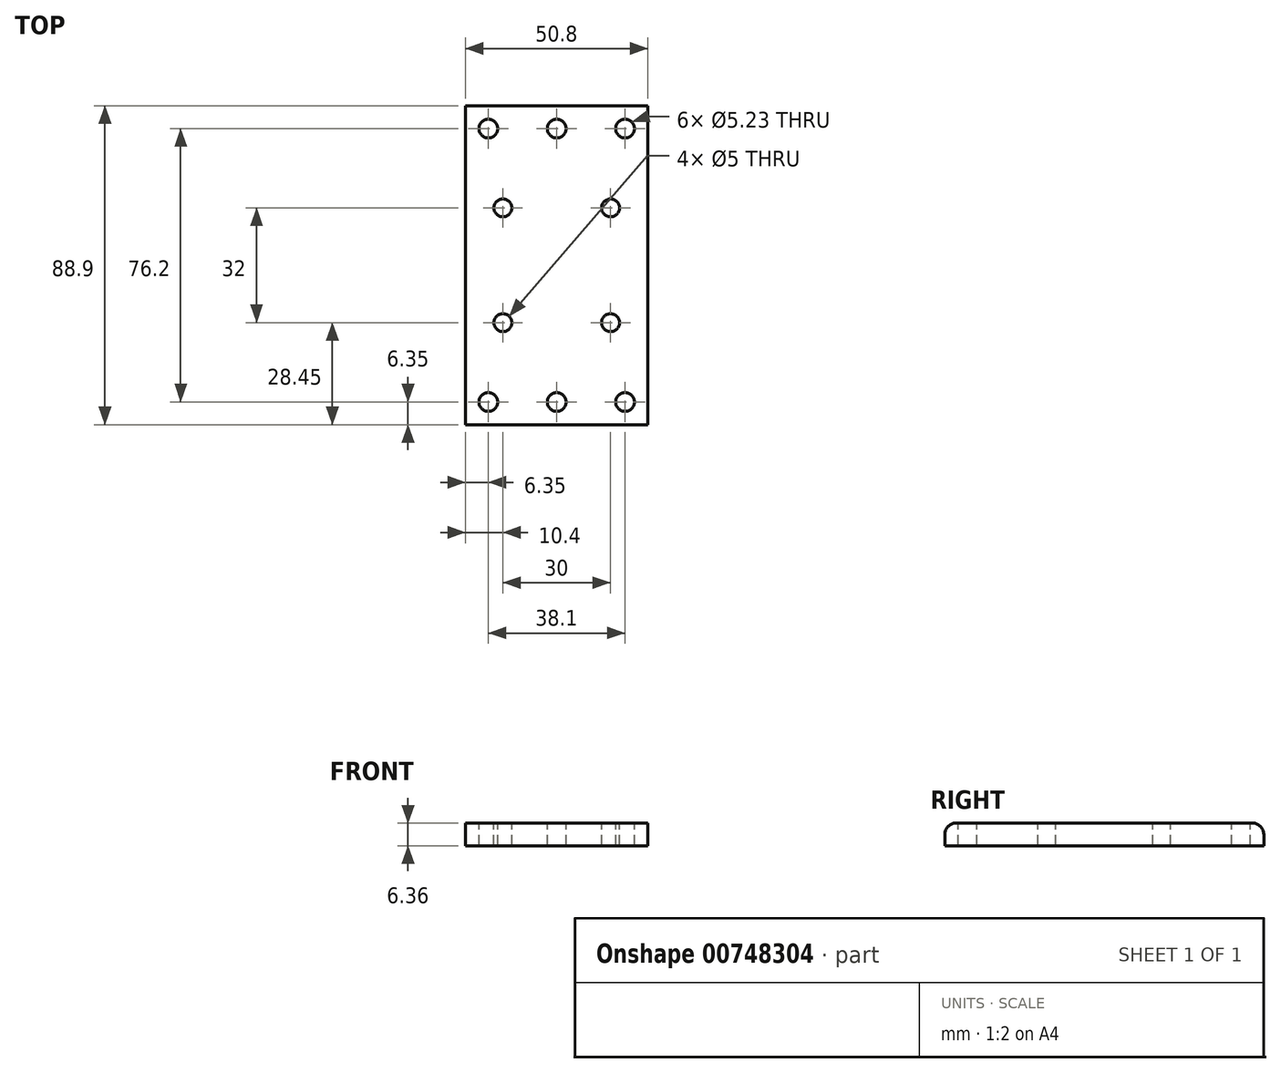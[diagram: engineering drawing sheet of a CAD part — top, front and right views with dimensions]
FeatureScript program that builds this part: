
annotation { "Feature Type Name" : "Feature", "Feature Type Description" : "" }
export const myFeature = defineFeature(function(context is Context, id is Id, definition is map)
    precondition{}
    {
        {
            var Q0;
            Q0=qCreatedBy(makeId("Front.planeOp"),FACE);
            var sketch = newSketch(context, id + "F0", { "sketchPlane" : qUnion([Q0])});
            skLineSegment(sketch, "E0.bottom", {"start": v(25.4, 3.18) * mm, "end": v(-25.4, 3.18) * mm});
            skLineSegment(sketch, "E0.top", {"start": v(25.4, -3.17) * mm, "end": v(-25.4, -3.17) * mm});
            skLineSegment(sketch, "E0.left", {"start": v(25.4, 3.18) * mm, "end": v(25.4, -3.17) * mm});
            skLineSegment(sketch, "E0.right", {"start": v(-25.4, 3.18) * mm, "end": v(-25.4, -3.17) * mm});
            skPoint(sketch, "E0.middle", {"position": v(0, 0) * mm});
            skSolve(sketch);
        }
        {
            var Q0;
            Q0 = qSketchRegion(id + "F0", true);
            extrude(context, id + "F1", {"entities" : qUnion([Q0]), "depth" : 88.9 * mm, "offsetDistance" : 25.4 * mm});
        }
        {
            var Q0;
            Q0=makeQuery(id+"F1.opExtrude","SWEPT_FACE",FACE,{"disambiguationData":[OSD([sQuery(id+"F0.wireOp",EDGE,"E0.bottom")])]});
            var sketch = newSketch(context, id + "F2", { "sketchPlane" : qUnion([Q0])});
            skLineSegment(sketch, "E1", {"start": v(0, -88.9) * mm, "end": v(0, 0) * mm, "construction": true});
            skLineSegment(sketch, "E2", {"start": v(-25.4, -44.45) * mm, "end": v(25.4, -44.45) * mm, "construction": true});
            skLineSegment(sketch, "E3.0", {"start": v(-25.4, -82.55) * mm, "end": v(25.4, -82.55) * mm, "construction": true});
            skLineSegment(sketch, "E4.0", {"start": v(-25.4, -6.35) * mm, "end": v(25.4, -6.35) * mm, "construction": true});
            skCircle(sketch, "E5", {"center": v(0, -82.55) * mm, "radius": 2.62 * mm});
            skCircle(sketch, "E6", {"center": v(0, -6.35) * mm, "radius": 2.62 * mm});
            skLineSegment(sketch, "E7.0", {"start": v(19.05, -88.9) * mm, "end": v(19.05, 12.7) * mm, "construction": true});
            skLineSegment(sketch, "E8.0", {"start": v(-19.05, -88.9) * mm, "end": v(-19.05, 12.7) * mm, "construction": true});
            skCircle(sketch, "E9", {"center": v(-19.05, -82.55) * mm, "radius": 2.62 * mm});
            skCircle(sketch, "E10", {"center": v(19.05, -82.55) * mm, "radius": 2.62 * mm});
            skCircle(sketch, "E11", {"center": v(19.05, -6.35) * mm, "radius": 2.62 * mm});
            skCircle(sketch, "E12", {"center": v(-19.05, -6.35) * mm, "radius": 2.62 * mm});
            skLineSegment(sketch, "E13.0", {"start": v(-25.4, -60.45) * mm, "end": v(25.4, -60.45) * mm, "construction": true});
            skLineSegment(sketch, "E14.0", {"start": v(-25.4, -28.45) * mm, "end": v(25.4, -28.45) * mm, "construction": true});
            skLineSegment(sketch, "E15.0", {"start": v(15, -88.9) * mm, "end": v(15, 12.7) * mm, "construction": true});
            skLineSegment(sketch, "E16.0", {"start": v(-15, -88.9) * mm, "end": v(-15, 12.7) * mm, "construction": true});
            skCircle(sketch, "E17", {"center": v(-15, -60.45) * mm, "radius": 2.5 * mm});
            skCircle(sketch, "E18", {"center": v(15, -60.45) * mm, "radius": 2.5 * mm});
            skCircle(sketch, "E19", {"center": v(15, -28.45) * mm, "radius": 2.5 * mm});
            skCircle(sketch, "E20", {"center": v(-15, -28.45) * mm, "radius": 2.5 * mm});
            skSolve(sketch);
        }
        {
            var Q0;
            Q0 = qSketchRegion(id + "F2", true);
            extrude(context, id + "F3", {"entities" : qUnion([Q0]), "operationType" : NewBodyOperationType.REMOVE, "endBound" : BoundingType.THROUGH_ALL, "oppositeDirection" : true, "depth" : 25.4 * mm, "offsetDistance" : 25.4 * mm});
        }
        {
            var Q0;
            Q0=makeQuery(id+"F1.opExtrude","CAP_EDGE",EDGE,{"disambiguationData":[OSD([sQuery(id+"F0.wireOp",EDGE,"E0.bottom")])],"isStart":true});
            var Q1;
            Q1=makeQuery(id+"F1.opExtrude","CAP_EDGE",EDGE,{"disambiguationData":[OSD([sQuery(id+"F0.wireOp",EDGE,"E0.bottom")])],"isStart":false});
            fillet(context, id + "F4", {"entities" : qUnion([Q0, Q1]), "radius" : 3.17 * mm, "tangentPropagation" : true, "allowEdgeOverflow" : false});
        }
    });
